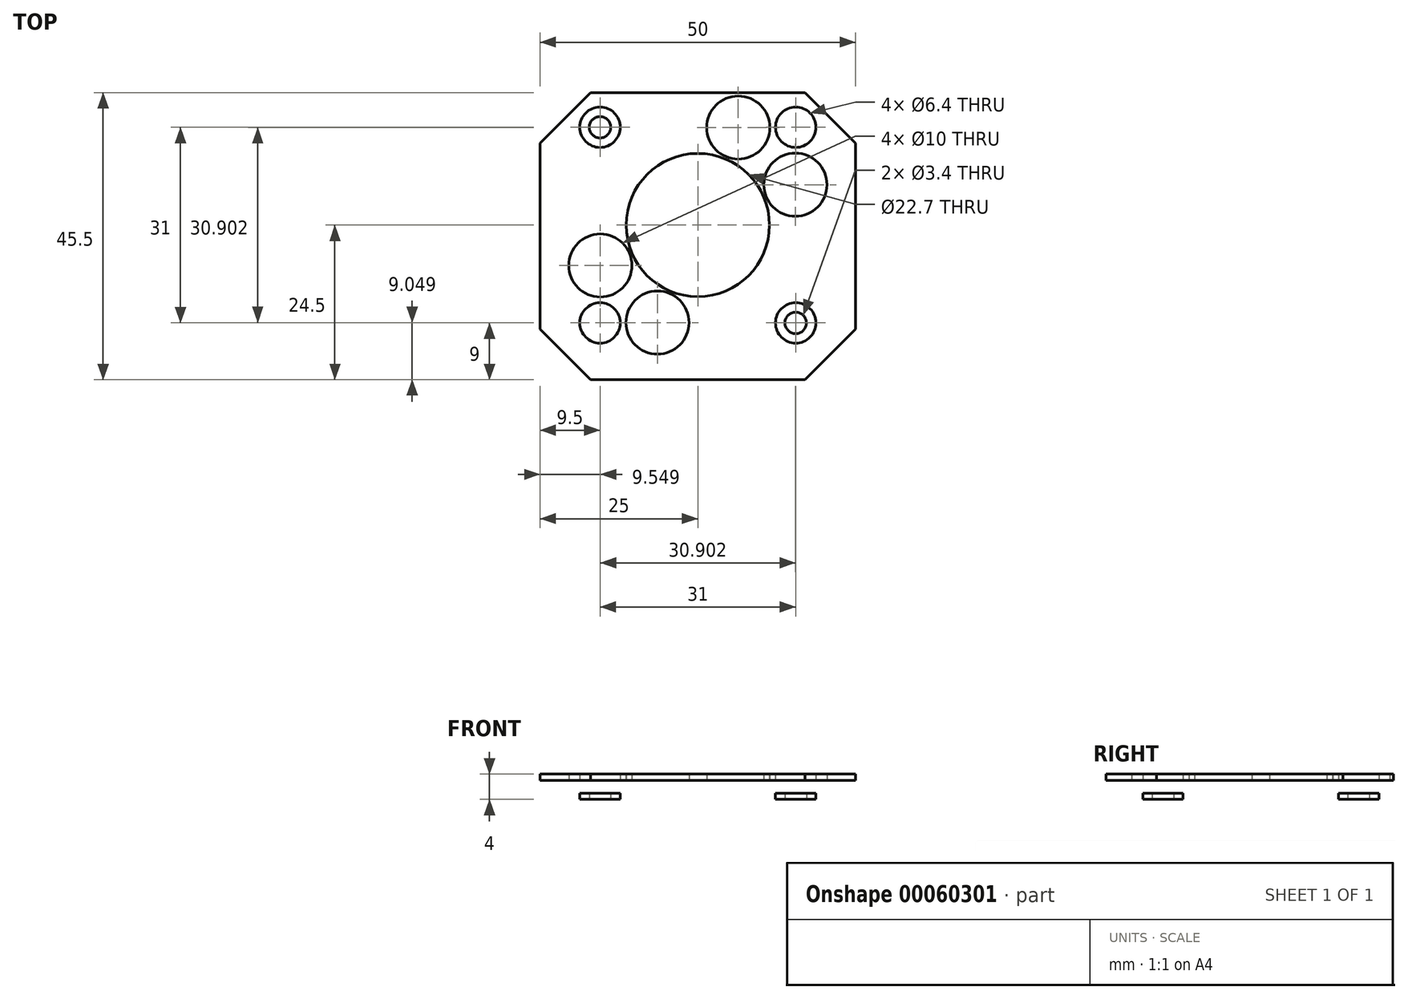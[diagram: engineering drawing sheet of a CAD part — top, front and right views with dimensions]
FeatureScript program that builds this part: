
annotation { "Feature Type Name" : "Feature", "Feature Type Description" : "" }
export const myFeature = defineFeature(function(context is Context, id is Id, definition is map)
    precondition{}
    {
        {
            var Q0;
            Q0=qCreatedBy(makeId("Top.planeOp"),FACE);
            var sketch = newSketch(context, id + "F0", { "sketchPlane" : qUnion([Q0])});
            skLineSegment(sketch, "E0.bottom", {"start": v(-25, 21) * mm, "end": v(25, 21) * mm});
            skLineSegment(sketch, "E0.top", {"start": v(-25, -24.5) * mm, "end": v(25, -24.5) * mm});
            skLineSegment(sketch, "E0.left", {"start": v(-25, 21) * mm, "end": v(-25, -24.5) * mm});
            skLineSegment(sketch, "E0.right", {"start": v(25, 21) * mm, "end": v(25, -24.5) * mm});
            skCircle(sketch, "E1", {"center": v(0, 0) * mm, "radius": 11.35 * mm});
            skCircle(sketch, "E2", {"center": v(-15.5, 15.5) * mm, "radius": 1.7 * mm});
            skCircle(sketch, "E3", {"center": v(-15.5, 15.5) * mm, "radius": 3.2 * mm});
            skLineSegment(sketch, "E4", {"start": v(0, 21) * mm, "end": v(0, -24.5) * mm, "construction": true});
            skPoint(sketch, "E5.center.orphan", {"position": v(-6.4, 15.45) * mm});
            skPoint(sketch, "E6.MirrorC.center.orphan", {"position": v(15.5, 15.5) * mm});
            skPoint(sketch, "E7.center.orphan", {"position": v(-15.45, 6.4) * mm});
            skPoint(sketch, "E8.MirrorC.center.orphan", {"position": v(-15.5, -15.5) * mm});
            skPoint(sketch, "E9.orphan", {"position": v(25, -1.75) * mm});
            skPoint(sketch, "E10.start.orphan", {"position": v(-25, -1.75) * mm});
            skLineSegment(sketch, "E11", {"start": v(0, 0) * mm, "end": v(-25, 0) * mm, "construction": true});
            skLineSegment(sketch, "E12", {"start": v(0, 0) * mm, "end": v(-25, 21) * mm, "construction": true});
            skCircle(sketch, "E13.MirrorC", {"center": v(-15.5, -15.5) * mm, "radius": 3.2 * mm});
            skCircle(sketch, "E14.MirrorC", {"center": v(-15.5, -15.5) * mm, "radius": 1.7 * mm});
            skCircle(sketch, "E15.MirrorC", {"center": v(15.5, 15.5) * mm, "radius": 3.2 * mm});
            skCircle(sketch, "E16.MirrorC", {"center": v(15.5, 15.5) * mm, "radius": 1.7 * mm});
            skCircle(sketch, "E17.MirrorC", {"center": v(15.5, -15.5) * mm, "radius": 1.7 * mm});
            skCircle(sketch, "E18.MirrorC", {"center": v(15.5, -15.5) * mm, "radius": 3.2 * mm});
            skCircle(sketch, "E19", {"center": v(-15.45, 6.4) * mm, "radius": 5 * mm});
            skCircle(sketch, "E20", {"center": v(-6.4, 15.45) * mm, "radius": 5 * mm});
            skCircle(sketch, "E21.MirrorC", {"center": v(6.4, 15.45) * mm, "radius": 5 * mm});
            skCircle(sketch, "E22.MirrorC", {"center": v(15.45, 6.4) * mm, "radius": 5 * mm});
            skCircle(sketch, "E23.MirrorC", {"center": v(15.45, -6.4) * mm, "radius": 5 * mm});
            skCircle(sketch, "E24.MirrorC", {"center": v(6.4, -15.45) * mm, "radius": 5 * mm});
            skCircle(sketch, "E25.MirrorC", {"center": v(-6.4, -15.45) * mm, "radius": 5 * mm});
            skCircle(sketch, "E26.MirrorC", {"center": v(-15.45, -6.4) * mm, "radius": 5 * mm});
            skSolve(sketch);
        }
        {
            var Q0;
            Q0 = qSketchRegion(id + "F0", true);
            var Q1;
            Q1=makeQuery(id+"F0.imprint","IMPRINT",FACE,{"disambiguationData":[TD([[makeQuery(id+"F0.imprint","IMPRINT",EDGE,{"derivedFrom":sQuery(id+"F0.wireOp",EDGE,"CukJmISx-E9ye-MpZz-U9hw-rAzSNoIQpnEC")}),1.0]])]});
            var Q2;
            Q2=makeQuery(id+"F0.imprint","IMPRINT",FACE,{"disambiguationData":[TD([[makeQuery(id+"F0.imprint","IMPRINT",EDGE,{"derivedFrom":sQuery(id+"F0.wireOp",EDGE,"a271242f-9b07-4c96-b2f1-4d94faa7b7b00.MirrorC")}),-1.0]])]});
            var Q3;
            Q3=makeQuery(id+"F0.imprint","IMPRINT",FACE,{"disambiguationData":[TD([[makeQuery(id+"F0.imprint","IMPRINT",EDGE,{"derivedFrom":sQuery(id+"F0.wireOp",EDGE,"0f4ff3c3-dedb-478a-988a-8fb6d9623b330.MirrorC")}),1.0]])]});
            var Q4;
            Q4=makeQuery(id+"F0.imprint","IMPRINT",FACE,{"disambiguationData":[TD([[makeQuery(id+"F0.imprint","IMPRINT",EDGE,{"derivedFrom":sQuery(id+"F0.wireOp",EDGE,"72d2942e-3dd9-4cb9-9d59-42ad35afa89c0.MirrorC")}),-1.0]])]});
            var Q5;
            Q5=makeQuery(id+"F0.imprint","IMPRINT",FACE,{"disambiguationData":[TD([[makeQuery(id+"F0.imprint","IMPRINT",EDGE,{"derivedFrom":sQuery(id+"F0.wireOp",EDGE,"6a968c77-9026-44df-8465-b83b1549f40f0.MirrorC")}),1.0]])]});
            var Q6;
            Q6=makeQuery(id+"F0.imprint","IMPRINT",FACE,{"disambiguationData":[TD([[makeQuery(id+"F0.imprint","IMPRINT",EDGE,{"derivedFrom":sQuery(id+"F0.wireOp",EDGE,"e2b3b2de-49e4-4749-b7db-a070f3c4161b0.MirrorC")}),-1.0]])]});
            var Q7;
            Q7=makeQuery(id+"F0.imprint","IMPRINT",FACE,{"disambiguationData":[TD([[makeQuery(id+"F0.imprint","IMPRINT",EDGE,{"derivedFrom":sQuery(id+"F0.wireOp",EDGE,"cb1a3495-648e-4739-8699-b75f58416e9e0.MirrorC")}),1.0]])]});
            var Q8;
            Q8=makeQuery(id+"F0.imprint","IMPRINT",FACE,{"disambiguationData":[TD([[makeQuery(id+"F0.imprint","IMPRINT",EDGE,{"derivedFrom":sQuery(id+"F0.wireOp",EDGE,"bd9026e0-8413-4caf-8576-213ec2bfc8dd0.MirrorC")}),-1.0]])]});
            var Q9;
            Q9=makeQuery(id+"F0.imprint","IMPRINT",FACE,{"disambiguationData":[TD([[makeQuery(id+"F0.imprint","IMPRINT",EDGE,{"derivedFrom":sQuery(id+"F0.wireOp",EDGE,"E26.MirrorC")}),-1.0]])]});
            var Q10;
            Q10=makeQuery(id+"F0.imprint","IMPRINT",FACE,{"disambiguationData":[TD([[makeQuery(id+"F0.imprint","IMPRINT",EDGE,{"derivedFrom":sQuery(id+"F0.wireOp",EDGE,"E25.MirrorC")}),-1.0]])]});
            var Q11;
            Q11=makeQuery(id+"F0.imprint","IMPRINT",FACE,{"disambiguationData":[TD([[makeQuery(id+"F0.imprint","IMPRINT",EDGE,{"derivedFrom":sQuery(id+"F0.wireOp",EDGE,"E24.MirrorC")}),1.0]])]});
            var Q12;
            Q12=makeQuery(id+"F0.imprint","IMPRINT",FACE,{"disambiguationData":[TD([[makeQuery(id+"F0.imprint","IMPRINT",EDGE,{"derivedFrom":sQuery(id+"F0.wireOp",EDGE,"E23.MirrorC")}),1.0]])]});
            var Q13;
            Q13=makeQuery(id+"F0.imprint","IMPRINT",FACE,{"disambiguationData":[TD([[makeQuery(id+"F0.imprint","IMPRINT",EDGE,{"derivedFrom":sQuery(id+"F0.wireOp",EDGE,"E22.MirrorC")}),-1.0]])]});
            var Q14;
            Q14=makeQuery(id+"F0.imprint","IMPRINT",FACE,{"disambiguationData":[TD([[makeQuery(id+"F0.imprint","IMPRINT",EDGE,{"derivedFrom":sQuery(id+"F0.wireOp",EDGE,"E21.MirrorC")}),-1.0]])]});
            var Q15;
            Q15=makeQuery(id+"F0.imprint","IMPRINT",FACE,{"disambiguationData":[TD([[makeQuery(id+"F0.imprint","IMPRINT",EDGE,{"derivedFrom":sQuery(id+"F0.wireOp",EDGE,"E20")}),1.0]])]});
            var Q16;
            Q16=makeQuery(id+"F0.imprint","IMPRINT",FACE,{"disambiguationData":[TD([[makeQuery(id+"F0.imprint","IMPRINT",EDGE,{"derivedFrom":sQuery(id+"F0.wireOp",EDGE,"E19")}),1.0]])]});
            extrude(context, id + "F1", {"entities" : qUnion([Q0, Q1, Q2, Q3, Q4, Q5, Q6, Q7, Q8, Q9, Q10, Q11, Q12, Q13, Q14, Q15, Q16]), "depth" : 4 * mm});
        }
        {
            var Q0;
            Q0=makeQuery(id+"F0.imprint","IMPRINT",FACE,{"disambiguationData":[TD([[makeQuery(id+"F0.imprint","IMPRINT",EDGE,{"derivedFrom":sQuery(id+"F0.wireOp",EDGE,"E2")}),-1.0]])]});
            var Q1;
            Q1=makeQuery(id+"F0.imprint","IMPRINT",FACE,{"disambiguationData":[TD([[makeQuery(id+"F0.imprint","IMPRINT",EDGE,{"derivedFrom":sQuery(id+"F0.wireOp",EDGE,"E15.MirrorC")}),-1.0]])]});
            var Q2;
            Q2=makeQuery(id+"F0.imprint","IMPRINT",FACE,{"disambiguationData":[TD([[makeQuery(id+"F0.imprint","IMPRINT",EDGE,{"derivedFrom":sQuery(id+"F0.wireOp",EDGE,"E17.MirrorC")}),-1.0]])]});
            var Q3;
            Q3=makeQuery(id+"F0.imprint","IMPRINT",FACE,{"disambiguationData":[TD([[makeQuery(id+"F0.imprint","IMPRINT",EDGE,{"derivedFrom":sQuery(id+"F0.wireOp",EDGE,"E13.MirrorC")}),-1.0]])]});
            extrude(context, id + "F2", {"entities" : qUnion([Q0, Q1, Q2, Q3]), "operationType" : NewBodyOperationType.ADD, "depth" : 1 * mm});
        }
        {
            var Q0;
            Q0=makeQuery(id+"F0.imprint","IMPRINT",FACE,{"disambiguationData":[TD([[makeQuery(id+"F0.imprint","IMPRINT",EDGE,{"derivedFrom":sQuery(id+"F0.wireOp",EDGE,"E26.MirrorC")}),-1.0]])]});
            var Q1;
            Q1=makeQuery(id+"F0.imprint","IMPRINT",FACE,{"disambiguationData":[TD([[makeQuery(id+"F0.imprint","IMPRINT",EDGE,{"derivedFrom":sQuery(id+"F0.wireOp",EDGE,"E25.MirrorC")}),-1.0]])]});
            var Q2;
            Q2=makeQuery(id+"F0.imprint","IMPRINT",FACE,{"disambiguationData":[TD([[makeQuery(id+"F0.imprint","IMPRINT",EDGE,{"derivedFrom":sQuery(id+"F0.wireOp",EDGE,"E24.MirrorC")}),1.0]])]});
            var Q3;
            Q3=makeQuery(id+"F0.imprint","IMPRINT",FACE,{"disambiguationData":[TD([[makeQuery(id+"F0.imprint","IMPRINT",EDGE,{"derivedFrom":sQuery(id+"F0.wireOp",EDGE,"E23.MirrorC")}),1.0]])]});
            var Q4;
            Q4=makeQuery(id+"F0.imprint","IMPRINT",FACE,{"disambiguationData":[TD([[makeQuery(id+"F0.imprint","IMPRINT",EDGE,{"derivedFrom":sQuery(id+"F0.wireOp",EDGE,"E22.MirrorC")}),-1.0]])]});
            var Q5;
            Q5=makeQuery(id+"F0.imprint","IMPRINT",FACE,{"disambiguationData":[TD([[makeQuery(id+"F0.imprint","IMPRINT",EDGE,{"derivedFrom":sQuery(id+"F0.wireOp",EDGE,"E21.MirrorC")}),-1.0]])]});
            var Q6;
            Q6=makeQuery(id+"F0.imprint","IMPRINT",FACE,{"disambiguationData":[TD([[makeQuery(id+"F0.imprint","IMPRINT",EDGE,{"derivedFrom":sQuery(id+"F0.wireOp",EDGE,"E20")}),1.0]])]});
            var Q7;
            Q7=makeQuery(id+"F0.imprint","IMPRINT",FACE,{"disambiguationData":[TD([[makeQuery(id+"F0.imprint","IMPRINT",EDGE,{"derivedFrom":sQuery(id+"F0.wireOp",EDGE,"E19")}),1.0]])]});
            extrude(context, id + "F3", {"entities" : qUnion([Q0, Q1, Q2, Q3, Q4, Q5, Q6, Q7]), "operationType" : NewBodyOperationType.REMOVE, "depth" : 3 * mm});
        }
        {
            var Q0;
            Q0=makeQuery(id+"F1.opExtrude","SWEPT_EDGE",EDGE,{"disambiguationData":[OSD([sQuery(id+"F0.wireOp",EDGE,"E0.bottom"),sQuery(id+"F0.wireOp",EDGE,"E0.right")])]});
            var Q1;
            Q1=makeQuery(id+"F1.opExtrude","SWEPT_EDGE",EDGE,{"disambiguationData":[OSD([sQuery(id+"F0.wireOp",EDGE,"E0.bottom"),sQuery(id+"F0.wireOp",EDGE,"E0.left"),sQuery(id+"F0.wireOp",EDGE,"ufooeJKY-fScE-udud-P1ru-SwBntJisfboj")])]});
            var Q2;
            Q2=makeQuery(id+"F1.opExtrude","SWEPT_EDGE",EDGE,{"disambiguationData":[OSD([sQuery(id+"F0.wireOp",EDGE,"E0.top"),sQuery(id+"F0.wireOp",EDGE,"E0.right")])]});
            var Q3;
            Q3=makeQuery(id+"F1.opExtrude","SWEPT_EDGE",EDGE,{"disambiguationData":[OSD([sQuery(id+"F0.wireOp",EDGE,"E0.top"),sQuery(id+"F0.wireOp",EDGE,"E0.left")])]});
            chamfer(context, id + "F4", {"entities" : qUnion([Q0, Q1, Q2, Q3]), "width" : 8 * mm, "tangentPropagation" : true});
        }
    });
